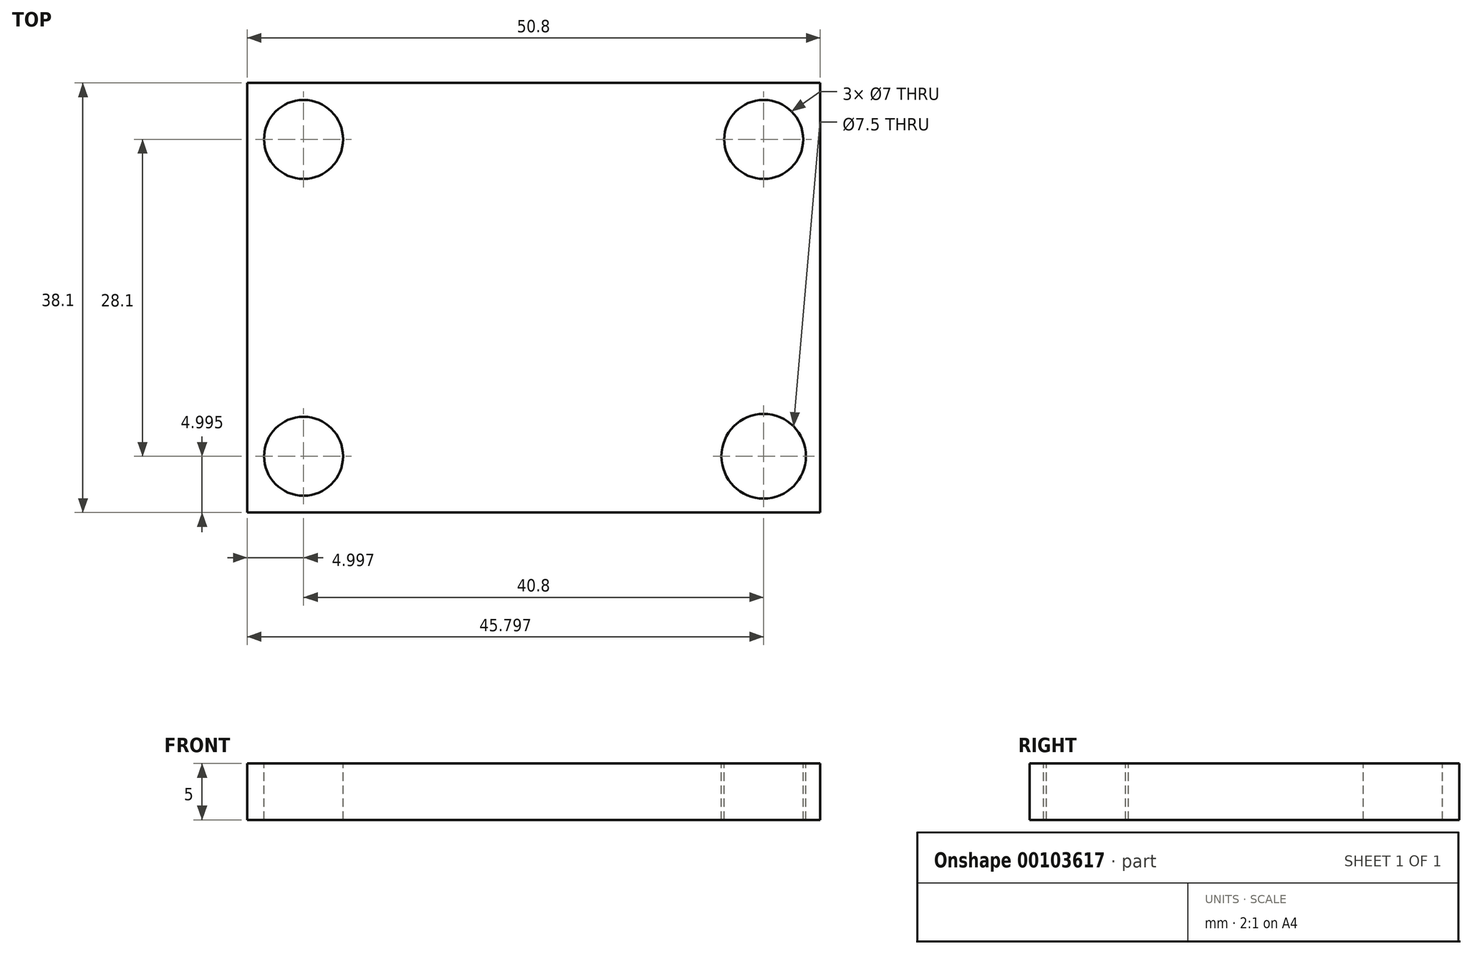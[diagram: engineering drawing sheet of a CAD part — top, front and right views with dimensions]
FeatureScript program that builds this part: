
annotation { "Feature Type Name" : "Feature", "Feature Type Description" : "" }
export const myFeature = defineFeature(function(context is Context, id is Id, definition is map)
    precondition{}
    {
        {
            var Q0;
            Q0=qCreatedBy(makeId("Top.planeOp"),FACE);
            var sketch = newSketch(context, id + "F0", { "sketchPlane" : qUnion([Q0])});
            skLineSegment(sketch, "E0.bottom", {"start": v(-32.92, 10.92) * mm, "end": v(17.88, 10.92) * mm});
            skLineSegment(sketch, "E0.top", {"start": v(-32.92, -27.18) * mm, "end": v(17.88, -27.18) * mm});
            skLineSegment(sketch, "E0.left", {"start": v(-32.92, 10.92) * mm, "end": v(-32.92, -27.18) * mm});
            skLineSegment(sketch, "E0.right", {"start": v(17.88, 10.92) * mm, "end": v(17.88, -27.18) * mm});
            skSolve(sketch);
        }
        {
            var Q0;
            Q0=makeQuery(id+"F0.imprint","IMPRINT",FACE,{"disambiguationData":[TD([[makeQuery(id+"F0.imprint","IMPRINT",EDGE,{"derivedFrom":sQuery(id+"F0.wireOp",EDGE,"E0.bottom")}),-1.0]])]});
            extrude(context, id + "F1", {"entities" : qUnion([Q0]), "depth" : 5 * mm});
        }
        {
            var Q0;
            Q0=makeQuery(id+"F1.opExtrude","CAP_FACE",FACE,{"disambiguationData":[OSD([sQuery(id+"F0.wireOp",EDGE,"E0.bottom"),sQuery(id+"F0.wireOp",EDGE,"E0.top"),sQuery(id+"F0.wireOp",EDGE,"E0.left"),sQuery(id+"F0.wireOp",EDGE,"E0.right")])],"isStart":false});
            var sketch = newSketch(context, id + "F2", { "sketchPlane" : qUnion([Q0])});
            skPoint(sketch, "E1", {"position": v(-27.92, -22.18) * mm});
            skCircle(sketch, "E2", {"center": v(-27.92, -22.18) * mm, "radius": 3.5 * mm});
            skPoint(sketch, "E3", {"position": v(-27.92, 5.92) * mm});
            skCircle(sketch, "E4", {"center": v(-27.92, 5.92) * mm, "radius": 3.5 * mm});
            skPoint(sketch, "E5", {"position": v(12.88, 5.92) * mm});
            skCircle(sketch, "E6", {"center": v(12.88, 5.92) * mm, "radius": 3.5 * mm});
            skPoint(sketch, "E7", {"position": v(12.88, -22.18) * mm});
            skCircle(sketch, "E8", {"center": v(12.88, -22.18) * mm, "radius": 3.75 * mm});
            skSolve(sketch);
        }
        {
            var Q0;
            Q0=makeQuery(id+"F2.imprint","IMPRINT",FACE,{"disambiguationData":[TD([[makeQuery(id+"F2.imprint","IMPRINT",EDGE,{"derivedFrom":sQuery(id+"F2.wireOp",EDGE,"E2")}),1.0]])]});
            var Q1;
            Q1=makeQuery(id+"F2.imprint","IMPRINT",FACE,{"disambiguationData":[TD([[makeQuery(id+"F2.imprint","IMPRINT",EDGE,{"derivedFrom":sQuery(id+"F2.wireOp",EDGE,"E6")}),1.0]])]});
            var Q2;
            Q2=makeQuery(id+"F2.imprint","IMPRINT",FACE,{"disambiguationData":[TD([[makeQuery(id+"F2.imprint","IMPRINT",EDGE,{"derivedFrom":sQuery(id+"F2.wireOp",EDGE,"E8")}),1.0]])]});
            var Q3;
            Q3=makeQuery(id+"F2.imprint","IMPRINT",FACE,{"disambiguationData":[TD([[makeQuery(id+"F2.imprint","IMPRINT",EDGE,{"derivedFrom":sQuery(id+"F2.wireOp",EDGE,"E4")}),1.0]])]});
            extrude(context, id + "F3", {"entities" : qUnion([Q0, Q1, Q2, Q3]), "operationType" : NewBodyOperationType.REMOVE, "oppositeDirection" : true, "depth" : 5 * mm});
        }
    });
